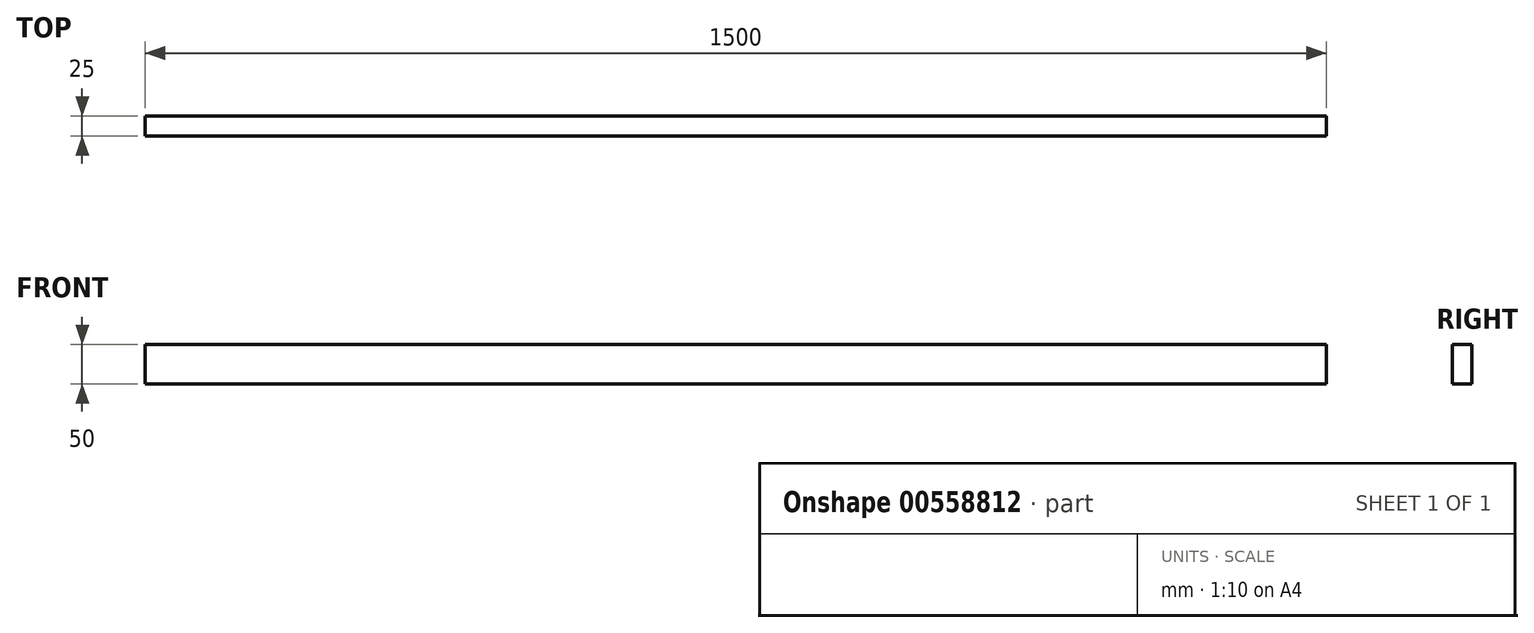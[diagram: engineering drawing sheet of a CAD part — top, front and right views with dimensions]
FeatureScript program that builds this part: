
annotation { "Feature Type Name" : "Feature", "Feature Type Description" : "" }
export const myFeature = defineFeature(function(context is Context, id is Id, definition is map)
    precondition{}
    {
        {
            var Q0;
            Q0=qCreatedBy(makeId("Right.planeOp"),FACE);
            var sketch = newSketch(context, id + "F0", { "sketchPlane" : qUnion([Q0])});
            skLineSegment(sketch, "E0.bottom", {"start": v(12.5, 25) * mm, "end": v(-12.5, 25) * mm});
            skLineSegment(sketch, "E0.top", {"start": v(12.5, -25) * mm, "end": v(-12.5, -25) * mm});
            skLineSegment(sketch, "E0.left", {"start": v(12.5, 25) * mm, "end": v(12.5, -25) * mm});
            skLineSegment(sketch, "E0.right", {"start": v(-12.5, 25) * mm, "end": v(-12.5, -25) * mm});
            skPoint(sketch, "E0.middle", {"position": v(0, 0) * mm});
            skSolve(sketch);
        }
        {
            var Q0;
            Q0 = qSketchRegion(id + "F0", true);
            extrude(context, id + "F1", {"entities" : qUnion([Q0]), "endBound" : BoundingType.SYMMETRIC, "depth" : 1500 * mm, "offsetDistance" : 25 * mm});
        }
    });
